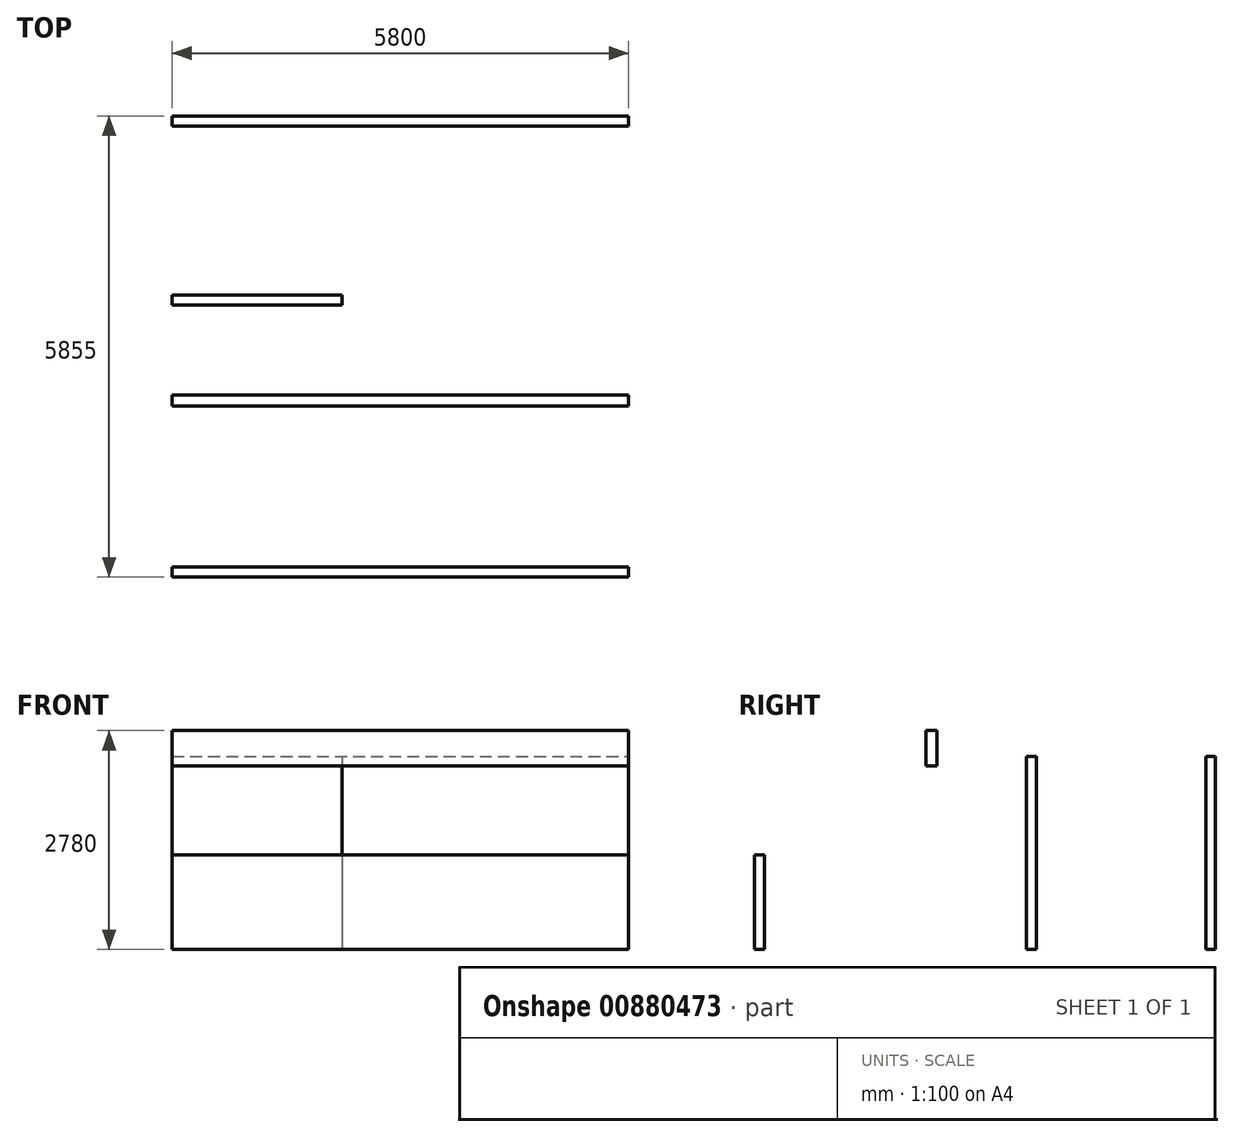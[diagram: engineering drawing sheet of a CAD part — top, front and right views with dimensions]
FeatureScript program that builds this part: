
annotation { "Feature Type Name" : "Feature", "Feature Type Description" : "" }
export const myFeature = defineFeature(function(context is Context, id is Id, definition is map)
    precondition{}
    {
        {
            var Q0;
            Q0=qCreatedBy(makeId("Top.planeOp"),FACE);
            var sketch = newSketch(context, id + "F0", { "sketchPlane" : qUnion([Q0])});
            skLineSegment(sketch, "E0.bottom", {"start": v(0, 0) * mm, "end": v(5800, 0) * mm});
            skLineSegment(sketch, "E0.top", {"start": v(0, 11060) * mm, "end": v(5800, 11060) * mm});
            skLineSegment(sketch, "E0.left", {"start": v(0, 0) * mm, "end": v(0, 11060) * mm});
            skLineSegment(sketch, "E0.right", {"start": v(5800, 0) * mm, "end": v(5800, 11060) * mm});
            skSolve(sketch);
        }
        {
            var Q0;
            Q0=makeQuery(id+"F0.imprint","IMPRINT",FACE,{"disambiguationData":[TD([[makeQuery(id+"F0.imprint","IMPRINT",EDGE,{"derivedFrom":sQuery(id+"F0.wireOp",EDGE,"E0.bottom")}),1.0]])]});
            var sketch = newSketch(context, id + "F1", { "sketchPlane" : qUnion([Q0])});
            skLineSegment(sketch, "E1.bottom", {"start": v(0, 1000) * mm, "end": v(5800, 1000) * mm});
            skLineSegment(sketch, "E1.top", {"start": v(0, 875) * mm, "end": v(5800, 875) * mm});
            skLineSegment(sketch, "E1.left", {"start": v(0, 1000) * mm, "end": v(0, 875) * mm});
            skLineSegment(sketch, "E1.right", {"start": v(5800, 1000) * mm, "end": v(5800, 875) * mm});
            skSolve(sketch);
        }
        {
            var Q0;
            Q0 = qSketchRegion(id + "F1", true);
            extrude(context, id + "F2", {"entities" : qUnion([Q0]), "depth" : 1200 * mm, "offsetDistance" : 25 * mm});
        }
        {
            var Q0;
            Q0=makeQuery(id+"F0.imprint","IMPRINT",FACE,{"disambiguationData":[TD([[makeQuery(id+"F0.imprint","IMPRINT",EDGE,{"derivedFrom":sQuery(id+"F0.wireOp",EDGE,"E0.bottom")}),1.0]])]});
            var sketch = newSketch(context, id + "F3", { "sketchPlane" : qUnion([Q0])});
            skLineSegment(sketch, "E2.bottom", {"start": v(0, 4455) * mm, "end": v(2160, 4455) * mm});
            skLineSegment(sketch, "E2.top", {"start": v(0, 4330) * mm, "end": v(2160, 4330) * mm});
            skLineSegment(sketch, "E2.left", {"start": v(0, 4455) * mm, "end": v(0, 4330) * mm});
            skLineSegment(sketch, "E2.right", {"start": v(2160, 4455) * mm, "end": v(2160, 4330) * mm});
            skSolve(sketch);
        }
        {
            var Q0;
            Q0 = qSketchRegion(id + "F3", true);
            extrude(context, id + "F4", {"entities" : qUnion([Q0]), "depth" : 2450 * mm, "offsetDistance" : 25 * mm});
        }
        {
            var Q0;
            Q0=makeQuery(id+"F0.imprint","IMPRINT",FACE,{"disambiguationData":[TD([[makeQuery(id+"F0.imprint","IMPRINT",EDGE,{"derivedFrom":sQuery(id+"F0.wireOp",EDGE,"E0.bottom")}),1.0]])]});
            var sketch = newSketch(context, id + "F5", { "sketchPlane" : qUnion([Q0])});
            skLineSegment(sketch, "E3.bottom", {"start": v(0, 3190) * mm, "end": v(5800, 3190) * mm});
            skLineSegment(sketch, "E3.top", {"start": v(0, 3050) * mm, "end": v(5800, 3050) * mm});
            skLineSegment(sketch, "E3.left", {"start": v(0, 3190) * mm, "end": v(0, 3050) * mm});
            skLineSegment(sketch, "E3.right", {"start": v(5800, 3190) * mm, "end": v(5800, 3050) * mm});
            skSolve(sketch);
        }
        {
            var Q0;
            Q0 = qSketchRegion(id + "F5", true);
            extrude(context, id + "F6", {"entities" : qUnion([Q0]), "depth" : 2780 * mm, "offsetDistance" : 25 * mm, "hasSecondDirection" : true, "secondDirectionOppositeDirection" : false, "secondDirectionDepth" : 2330 * mm});
        }
        {
            var Q0;
            Q0=makeQuery(id+"F0.imprint","IMPRINT",FACE,{"disambiguationData":[TD([[makeQuery(id+"F0.imprint","IMPRINT",EDGE,{"derivedFrom":sQuery(id+"F0.wireOp",EDGE,"E0.bottom")}),1.0]])]});
            var sketch = newSketch(context, id + "F7", { "sketchPlane" : qUnion([Q0])});
            skLineSegment(sketch, "E4.bottom", {"start": v(0, 6730) * mm, "end": v(5800, 6730) * mm});
            skLineSegment(sketch, "E4.top", {"start": v(0, 6605) * mm, "end": v(5800, 6605) * mm});
            skLineSegment(sketch, "E4.left", {"start": v(0, 6730) * mm, "end": v(0, 6605) * mm});
            skLineSegment(sketch, "E4.right", {"start": v(5800, 6730) * mm, "end": v(5800, 6605) * mm});
            skSolve(sketch);
        }
        {
            var Q0;
            Q0 = qSketchRegion(id + "F7", true);
            extrude(context, id + "F8", {"entities" : qUnion([Q0]), "depth" : 2450 * mm, "offsetDistance" : 25 * mm});
        }
    });
